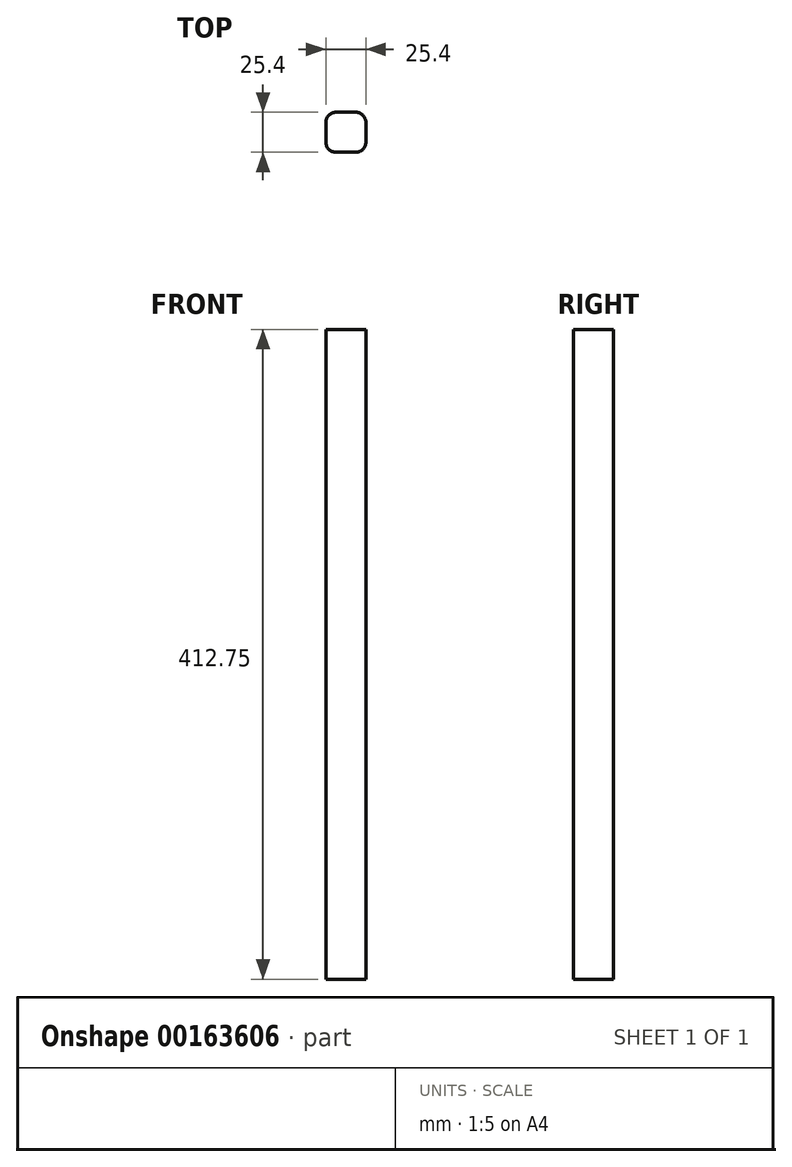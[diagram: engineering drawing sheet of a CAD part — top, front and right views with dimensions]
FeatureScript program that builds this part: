
annotation { "Feature Type Name" : "Feature", "Feature Type Description" : "" }
export const myFeature = defineFeature(function(context is Context, id is Id, definition is map)
    precondition{}
    {
        {
            var Q0;
            Q0=qCreatedBy(makeId("Top.planeOp"),FACE);
            var sketch = newSketch(context, id + "F0", { "sketchPlane" : qUnion([Q0])});
            skLineSegment(sketch, "E0.bottom", {"start": v(6.35, 12.7) * mm, "end": v(-6.35, 12.7) * mm});
            skLineSegment(sketch, "E0.top", {"start": v(6.35, -12.7) * mm, "end": v(-6.35, -12.7) * mm});
            skLineSegment(sketch, "E0.left", {"start": v(12.7, 6.35) * mm, "end": v(12.7, -6.35) * mm});
            skLineSegment(sketch, "E0.right", {"start": v(-12.7, 6.35) * mm, "end": v(-12.7, -6.35) * mm});
            skPoint(sketch, "E0.middle", {"position": v(0, 0) * mm});
            skPoint(sketch, "E1.visualSharp", {"position": v(-12.7, 12.7) * mm});
            skArc(sketch, "E1.filletArc", {"start": v(-6.35, 12.7) * mm, "mid": v(-10.84, 10.84) * mm, "end": v(-12.7, 6.35) * mm});
            skPoint(sketch, "E2.visualSharp", {"position": v(12.7, 12.7) * mm});
            skArc(sketch, "E2.filletArc", {"start": v(12.7, 6.35) * mm, "mid": v(10.84, 10.84) * mm, "end": v(6.35, 12.7) * mm});
            skPoint(sketch, "E3.visualSharp", {"position": v(12.7, -12.7) * mm});
            skArc(sketch, "E3.filletArc", {"start": v(6.35, -12.7) * mm, "mid": v(10.84, -10.84) * mm, "end": v(12.7, -6.35) * mm});
            skPoint(sketch, "E4.visualSharp", {"position": v(-12.7, -12.7) * mm});
            skArc(sketch, "E4.filletArc", {"start": v(-12.7, -6.35) * mm, "mid": v(-10.84, -10.84) * mm, "end": v(-6.35, -12.7) * mm});
            skSolve(sketch);
        }
        {
            var Q0;
            Q0=qSketchRegion(id+"F0",true);
            extrude(context, id + "F1", {"entities" : qUnion([Q0]), "depth" : 412.75 * mm, "offsetDistance" : 25.4 * mm});
        }
    });
